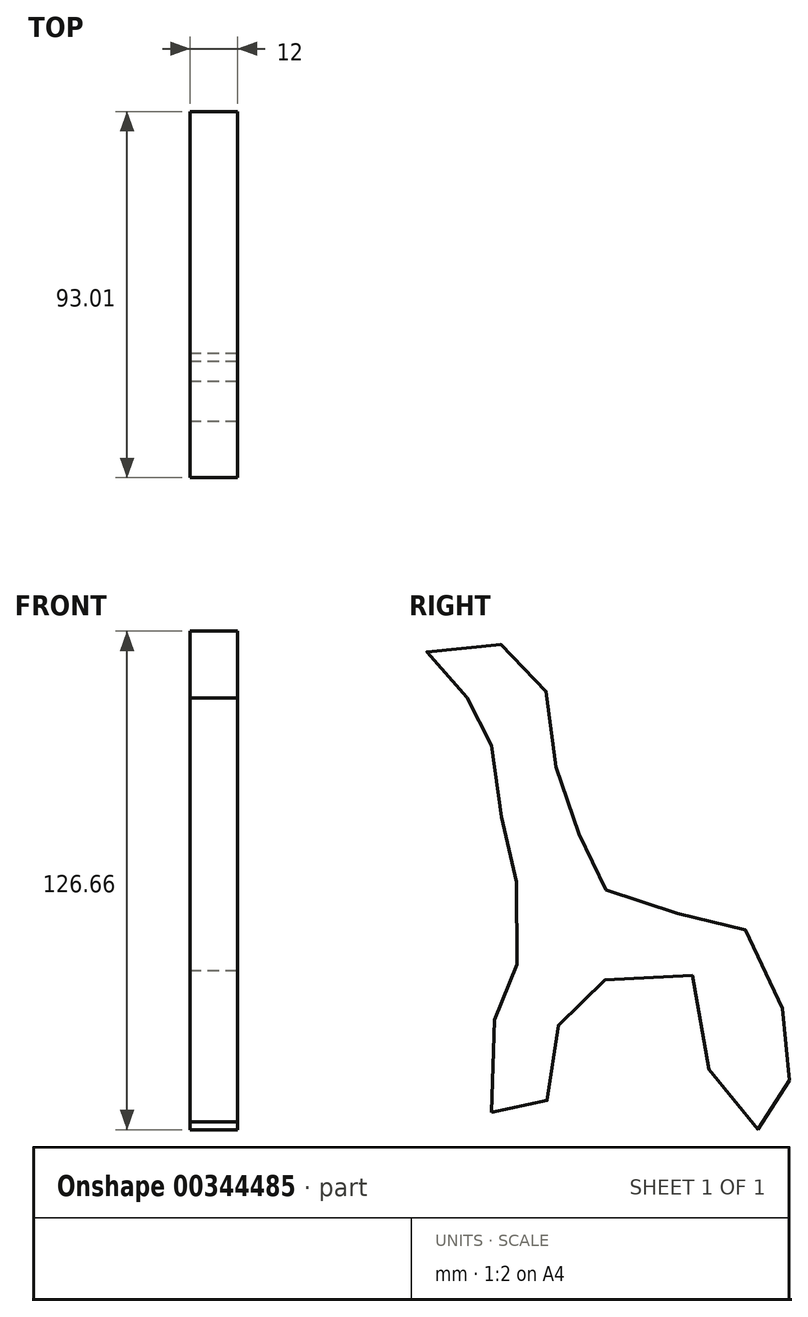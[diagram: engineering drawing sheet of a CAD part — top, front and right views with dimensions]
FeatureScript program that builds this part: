
annotation { "Feature Type Name" : "Feature", "Feature Type Description" : "" }
export const myFeature = defineFeature(function(context is Context, id is Id, definition is map)
    precondition{}
    {
        {
            var Q0;
            Q0=qCreatedBy(makeId("Right.planeOp"),FACE);
            var sketch = newSketch(context, id + "F0", { "sketchPlane" : qUnion([Q0])});
            skFitSpline(sketch, "E0", {"points": [v(-49.27, -59.48) * mm, v(-49.27, -38.56) * mm, v(-45.46, -29.05) * mm, v(-42.61, -21.45) * mm, v(-42.14, -5.28) * mm, v(-45.46, 8.5) * mm, v(-46.9, 16.58) * mm, v(-48.8, 28.94) * mm, v(-50.22, 40.35) * mm, v(-53.55, 45.58) * mm, v(-63.53, 47) * mm, v(-64, 60.8) * mm, v(-47.84, 59.84) * mm, v(-36.9, 51.76) * mm, v(-35, 44.63) * mm, v(-33.1, 29.42) * mm, v(-31.2, 21.81) * mm, v(-25.5, 7.08) * mm, v(-22.65, 0) * mm, v(-14.56, -6.7) * mm, v(0, -9.09) * mm, v(10.63, -10.51) * mm, v(22.52, -21.92) * mm, v(24.9, -39.99) * mm, v(26.32, -50.44) * mm, v(25.84, -59.48) * mm, v(15.38, -63.76) * mm, v(6.35, -50.92) * mm, v(3.5, -26.2) * mm, v(-11.71, -24.3) * mm, v(-26.92, -28.58) * mm, v(-32.15, -37.13) * mm, v(-36.43, -52.35) * mm, v(-35, -59.95) * mm, v(-49.27, -59.48) * mm]});
            skSolve(sketch);
        }
        {
            var Q0;
            Q0=makeQuery(id+"F0.imprint","IMPRINT",FACE,{"disambiguationData":[TD([[makeQuery(id+"F0.imprint","IMPRINT",EDGE,{"derivedFrom":sQuery(id+"F0.wireOp",EDGE,"E0")}),-1.0]])]});
            extrude(context, id + "F1", {"entities" : qUnion([Q0]), "depth" : 12 * mm});
        }
        {
            var Q0;
            Q0=qCreatedBy(makeId("Right.planeOp"),FACE);
            cPlane(context, id + "F2", {"entities" : qUnion([Q0]), "cplaneType" : CPlaneType.OFFSET, "offset" : 100 * mm, "oppositeDirection" : true, "width" : 150 * mm, "height" : 150 * mm});
        }
    });
